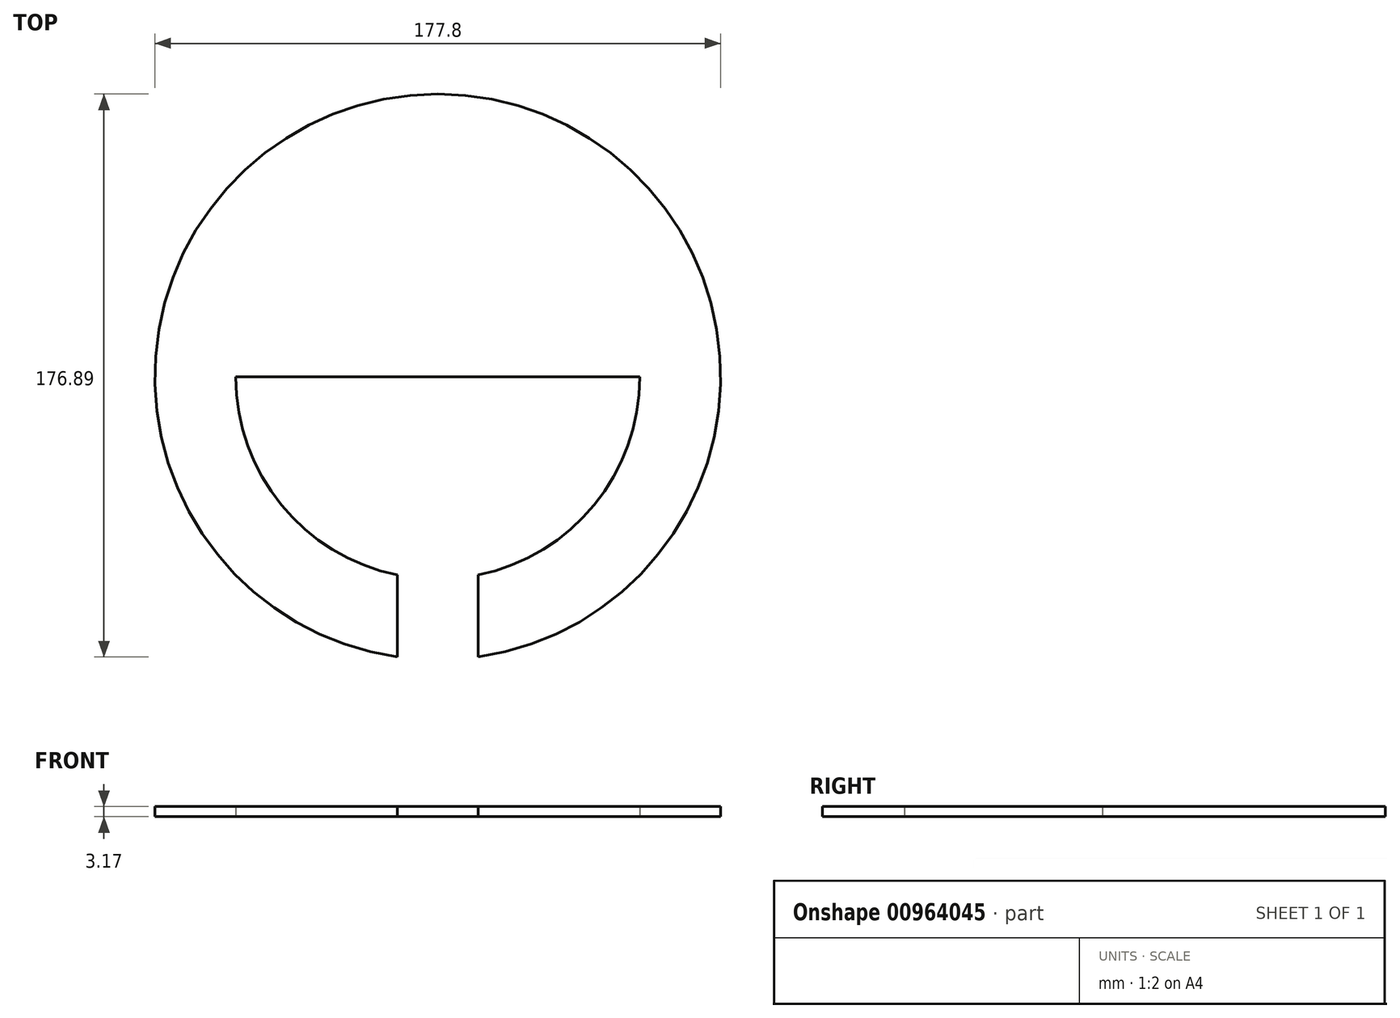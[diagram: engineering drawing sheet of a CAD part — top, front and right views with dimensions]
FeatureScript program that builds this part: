
annotation { "Feature Type Name" : "Feature", "Feature Type Description" : "" }
export const myFeature = defineFeature(function(context is Context, id is Id, definition is map)
    precondition{}
    {
        {
            var Q0;
            Q0=qCreatedBy(makeId("Top.planeOp"),FACE);
            var sketch = newSketch(context, id + "F0", { "sketchPlane" : qUnion([Q0])});
            skCircle(sketch, "E0", {"center": v(0, 0) * mm, "radius": 88.9 * mm});
            skCircle(sketch, "E1", {"center": v(0, 0) * mm, "radius": 63.5 * mm});
            skLineSegment(sketch, "E2", {"start": v(-63.5, 0) * mm, "end": v(63.5, 0) * mm});
            skSolve(sketch);
        }
        {
            var Q0;
            Q0=makeQuery(id+"F0.imprint","IMPRINT",FACE,{"disambiguationData":[TD([[makeQuery(id+"F0.imprint","IMPRINT",EDGE,{"derivedFrom":sQuery(id+"F0.wireOp",EDGE,"E0")}),1.0]])]});
            var Q1;
            {var subQ0=sQuery(id+"F0.wireOp",EDGE,"E2");Q1=makeQuery(id+"F0.imprint","IMPRINT",FACE,{"disambiguationData":[TD([[makeQuery(id+"F0.imprint","IMPRINT",EDGE,{"derivedFrom":subQ0}),1.0]])]});}
            extrude(context, id + "F1", {"entities" : qUnion([Q0, Q1]), "depth" : 3.17 * mm, "offsetDistance" : 25.4 * mm});
        }
        {
            var Q0;
            Q0=makeQuery(id+"F1.opExtrude","CAP_FACE",FACE,{"disambiguationData":[OSD([sQuery(id+"F0.wireOp",EDGE,"E0"),sQuery(id+"F0.wireOp",EDGE,"E1"),sQuery(id+"F0.wireOp",EDGE,"E2")])],"isStart":false});
            var sketch = newSketch(context, id + "F2", { "sketchPlane" : qUnion([Q0])});
            skLineSegment(sketch, "E3", {"start": v(0, -58.6) * mm, "end": v(-12.7, -58.6) * mm});
            skLineSegment(sketch, "E4", {"start": v(-12.7, -58.6) * mm, "end": v(-12.7, -96.49) * mm});
            skLineSegment(sketch, "E5", {"start": v(-12.7, -96.49) * mm, "end": v(12.7, -96.49) * mm});
            skLineSegment(sketch, "E6", {"start": v(12.7, -96.49) * mm, "end": v(12.7, -58.6) * mm});
            skLineSegment(sketch, "E7", {"start": v(12.7, -58.6) * mm, "end": v(0, -58.6) * mm});
            skSolve(sketch);
        }
        {
            var Q0;
            Q0 = qSketchRegion(id + "F2", true);
            extrude(context, id + "F3", {"entities" : qUnion([Q0]), "operationType" : NewBodyOperationType.REMOVE, "oppositeDirection" : true, "depth" : 6.35 * mm, "offsetDistance" : 25.4 * mm});
        }
    });
